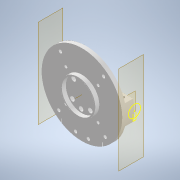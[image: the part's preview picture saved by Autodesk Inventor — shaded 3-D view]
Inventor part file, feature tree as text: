
AUTODESK INVENTOR PART (.ipt)
format: ipt  version: 2021 (Build 250183000, 183)  size: 418,304 bytes
history: native  units: mm
features: reference x31, other x21, sketch x18, extrude x16, direct_edit x14, move_body x5, plane x3, mirror x2, projected_geometry x1
ambient origin geometry x8: Origin, YZ Plane, XZ Plane, XY Plane, X Axis, Y Axis, Z Axis, Center Point
bodies: Solid1 (feature_tree)
feature tree (111):
  extrude  "Extrusion1"  Depth=5.0mm TaperAngle=0.0deg
  extrude  "Extrusion2"  Depth=43.0mm
  extrude  "Extrusion3"  Depth=3.0mm TaperAngle=0.0deg
  extrude  "Extrusion4"  Depth=10.0mm TaperAngle=0.0deg
  extrude  "Extrusion5"  Depth=5.0mm
  extrude  "Extrusion6"  Depth=3.2mm
  plane  "Work Plane1"
  plane  "Work Plane2"
  sketch  "Sketch10"  dims[d29=28.0mm d30=0.0mm d31=10.0mm d32=0.0mm]
  sketch  "Sketch11"  dims[d33=2.0mm d49=0.0mm d50=0.0mm]
  plane  "Work Plane3"
  extrude  "Extrusion10"  Depth=28.0mm TaperAngle=0.0deg
  extrude  "Extrusion11"  Depth=10.0mm TaperAngle=0.0deg
  mirror  "Mirror3"
  extrude  "Extrusion12"  TaperAngle=0.0deg  [1 undecoded]
  extrude  "Extrusion13"  Depth=5.0mm
  extrude  "Extrusion14"  [1 undecoded]
  direct_edit  "Direct Edit1"
  extrude  "Extrusion15"  Depth=33.0mm
  direct_edit  "Direct Edit2"
  extrude  "Extrusion16"  Depth=4.0mm
  direct_edit  "Direct Edit3"
  extrude  "Extrusion17"  [1 undecoded]
  direct_edit  "Direct Edit4"
  direct_edit  "Direct Edit5"
  direct_edit  "Direct Edit6"
  direct_edit  "Direct Edit7"
  direct_edit  "Direct Edit8"
  mirror  "Mirror4"
  direct_edit  "Direct Edit9"
  direct_edit  "Direct Edit10"
  direct_edit  "Direct Edit11"
  direct_edit  "Direct Edit12"
  direct_edit  "Direct Edit13"
  direct_edit  "Direct Edit14"
  extrude  "Extrusion18"  TaperAngle=0.0deg  [1 undecoded]
  extrude  "Extrusion19"  [1 undecoded]
  sketch  "Sketch1"  dims[d0=10.0mm d1=0.0mm d2=5.0mm d3=0.0mm]
  reference  "Reference1"
  sketch  "Sketch2"  dims[d4=17.25mm d5=0.0mm d6=43.0mm]
  reference  "Reference2"
  reference  "Reference3"
  sketch  "Sketch3"  dims[d7=40.0mm d8=3.0mm d9=0.0mm]
  reference  "Reference4"
  reference  "Reference5"
  reference  "Reference6"
  reference  "Reference7"
  reference  "Reference8"
  reference  "Reference9"
  reference  "Reference10"
  reference  "Reference11"
  sketch  "Sketch4"  dims[d10=10.0mm d11=0.0mm d12=10.0mm d13=0.0mm]
  reference  "Reference12"
  sketch  "Sketch6"  dims[d20=5.0mm d21=0.0mm d22=5.0mm]
  reference  "Reference15"
  reference  "Reference16"
  sketch  "Sketch7"  dims[d23=8.0mm d24=3.2mm]
  projected_geometry  "Projected Loop1"
  sketch  "Sketch9"  dims[d25=0.0mm d26=0.0mm d27=28.0mm d28=0.0mm]
  reference  "Reference27"
  reference  "Reference28"
  reference  "Reference29"
  reference  "Reference30"
  reference  "Reference31"
  reference  "Reference32"
  reference  "Reference33"
  reference  "Reference34"
  sketch  "Sketch13"  dims[d51=5.0mm d52=5.0mm]
  sketch  "Sketch14"  dims[d53=2.0mm d54=0.0mm d55=-2.0mm]
  sketch  "Sketch15"  dims[d56=85.0mm d57=33.0mm]
  reference  "Reference35"
  reference  "Reference36"
  reference  "Reference37"
  reference  "Reference38"
  reference  "Reference39"
  reference  "Reference40"
  reference  "Reference41"
  reference  "Reference42"
  sketch  "Sketch16"  dims[d58=4.0mm d59=4.0mm]
  sketch  "Sketch17"  dims[d60=0.0mm d61=0.0mm d62=-0.5mm]
  sketch  "Sketch18"  dims[d63=0.0mm d64=-1.5mm d65=0.0mm d66=0.0mm d67=-1.0mm d68=0.0mm]
  sketch  "Sketch19"  dims[d69=-0.5mm d70=-0.25mm]
  sketch  "Sketch20"  dims[d71=-2.0mm d72=-2.0mm d73=0.0mm]
  sketch  "Sketch21"  dims[d74=0.0mm d75=0.0mm d76=-2.25mm d77=0.0mm d78=0.0mm d79=-2.0mm d80=-0.5mm d81=2.0mm d82=-2.0mm d83=-2.0mm d84=10.0mm d85=0.0mm d86=10.0mm d87=0.0mm d16=0.5mm d17=0.872665mm d18=0.5mm d19=0.872665mm]
  reference  "Reference45"
  parser-record x3  (decoder bookkeeping rows leaked as tree rows — omitted from the tree; the rows remain in map.json)
  other  "whole_assembly.iam"
  other  "tool_holder:1"
  other  "robot_with_gripper.iam"
  other  "IRB120_3-58_IRC5_rev1:1"
  other  "IRB120_3-58_IRC5_Link6_rev1_6"
  other  "539636 HGP-16-A-B-SSK---(asm_0_-ZH):1"
  other  "gripper extension:1"
  other  "Size1"
  other  "Delete1"
  other  "Size2"
  other  "Size3"
  move_body  "Move1"
  move_body  "Move2"
  other  "Size4"
  other  "Size5"
  move_body  "Move3"
  move_body  "Move4"
  move_body  "Move5"
  other  "Size6"
  other  "Size7"
  other  "Size8"
  other  "Size9"
  other  "Assembly1.iam"
note: 5 required parameter values undecoded (feature->parameter linkage not recoverable at this tier; creation-order binding heuristic only, values carry confidence <= 0.55)
note: 3 file-system paths scrubbed to <path> (originals preserved in map.json)
